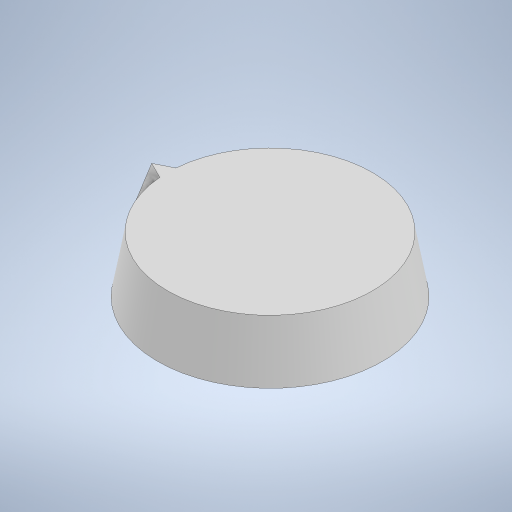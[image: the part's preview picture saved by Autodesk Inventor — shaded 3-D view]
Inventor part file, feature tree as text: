
AUTODESK INVENTOR PART (.ipt)
format: ipt  version: 2023 (Build 270158030, 158C)  size: 226,304 bytes
history: native  units: in
note: dims shown in document units (in); Inventor stores cm internally (conversion verified against a paired STEP export)
features: extrude x2, sketch x2
ambient origin geometry x8: Origin, YZ Plane, XZ Plane, XY Plane, X Axis, Y Axis, Z Axis, Center Point
bodies: Solid1 (feature_tree)
feature tree (4):
  extrude  "Extrusion1"  Depth=0.125in
  extrude  "Extrusion2"  Depth=0.05in
  sketch  "Sketch1"  dims[d0=0.4in d1=0.125in]
  sketch  "Sketch2"  dims[d2=0.125in d3=0.5in d4=0.25in d5=0.1in d6=-0.0687in d7=0.1in d8=0.05in d9=0.0in]
